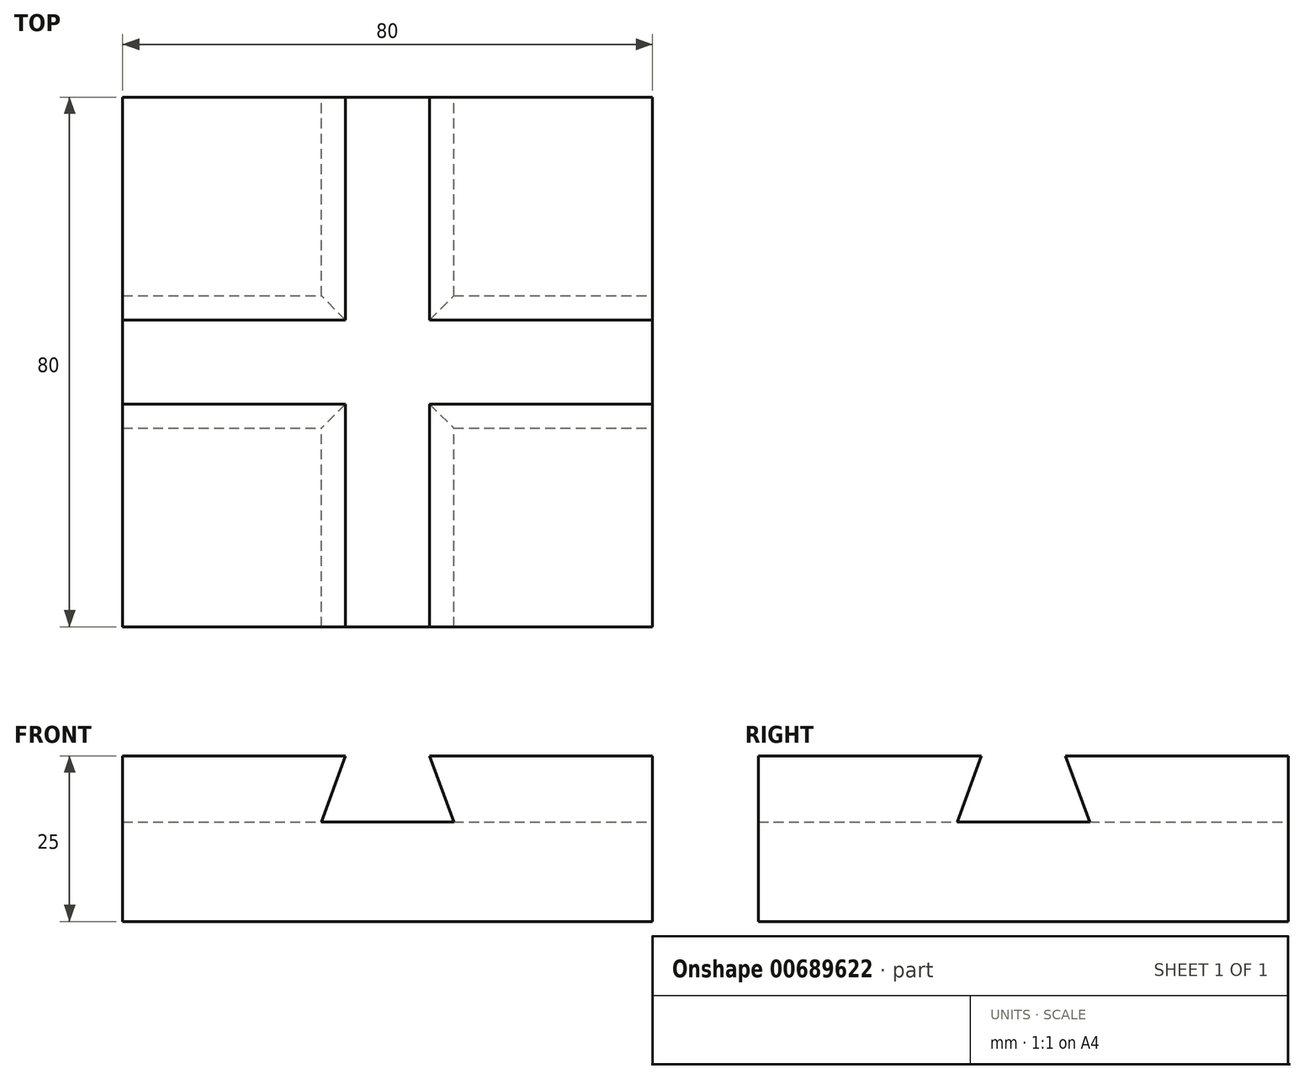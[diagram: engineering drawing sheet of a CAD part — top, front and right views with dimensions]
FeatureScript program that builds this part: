
annotation { "Feature Type Name" : "Feature", "Feature Type Description" : "" }
export const myFeature = defineFeature(function(context is Context, id is Id, definition is map)
    precondition{}
    {
        {
            var Q0;
            Q0=qCreatedBy(makeId("Front.planeOp"),FACE);
            var sketch = newSketch(context, id + "F0", { "sketchPlane" : qUnion([Q0])});
            skLineSegment(sketch, "E0.bottom", {"start": v(-11.36, -2.73) * mm, "end": v(-91.36, -2.73) * mm});
            skLineSegment(sketch, "E0.top", {"start": v(-11.36, 22.27) * mm, "end": v(-45, 22.27) * mm});
            skLineSegment(sketch, "E0.left", {"start": v(-11.36, -2.73) * mm, "end": v(-11.36, 22.27) * mm});
            skLineSegment(sketch, "E0.right", {"start": v(-91.36, -2.73) * mm, "end": v(-91.36, 22.27) * mm});
            skLineSegment(sketch, "E1.bottom", {"start": v(-61.36, 12.27) * mm, "end": v(-41.36, 12.27) * mm});
            skLineSegment(sketch, "E2", {"start": v(-57.72, 22.27) * mm, "end": v(-61.36, 12.27) * mm});
            skLineSegment(sketch, "E3", {"start": v(-45, 22.27) * mm, "end": v(-41.36, 12.27) * mm});
            skLineSegment(sketch, "E4.trimOffspring", {"start": v(-57.72, 22.27) * mm, "end": v(-91.36, 22.27) * mm});
            skSolve(sketch);
        }
        {
            var Q0;
            Q0=makeQuery(id+"F0.imprint","IMPRINT",FACE,{"disambiguationData":[TD([[makeQuery(id+"F0.imprint","IMPRINT",EDGE,{"derivedFrom":sQuery(id+"F0.wireOp",EDGE,"E0.bottom")}),-1.0]])]});
            extrude(context, id + "F1", {"entities" : qUnion([Q0]), "depth" : 80 * mm, "offsetDistance" : 25 * mm});
        }
        {
            var Q0;
            Q0=makeQuery(id+"F1.opExtrude","SWEPT_FACE",FACE,{"disambiguationData":[OSD([sQuery(id+"F0.wireOp",EDGE,"E0.left")])]});
            var sketch = newSketch(context, id + "F2", { "sketchPlane" : qUnion([Q0])});
            skLineSegment(sketch, "E5.bottom", {"start": v(-50, 12.27) * mm, "end": v(-30, 12.27) * mm});
            skPoint(sketch, "E5.middle", {"position": v(-40, 22.27) * mm});
            skLineSegment(sketch, "E6", {"start": v(-40, 22.27) * mm, "end": v(-46.36, 22.27) * mm});
            skLineSegment(sketch, "E7", {"start": v(-40, 22.27) * mm, "end": v(-33.64, 22.27) * mm});
            skLineSegment(sketch, "E8", {"start": v(-46.36, 22.27) * mm, "end": v(-50, 12.27) * mm});
            skLineSegment(sketch, "E9", {"start": v(-33.64, 22.27) * mm, "end": v(-30, 12.27) * mm});
            skSolve(sketch);
        }
        {
            var Q0;
            Q0=makeQuery(id+"F2.imprint","IMPRINT",FACE,{"disambiguationData":[TD([[makeQuery(id+"F2.imprint","IMPRINT",EDGE,{"derivedFrom":sQuery(id+"F2.wireOp",EDGE,"E5.bottom")}),1.0]])]});
            extrude(context, id + "F3", {"entities" : qUnion([Q0]), "operationType" : NewBodyOperationType.REMOVE, "oppositeDirection" : true, "depth" : 80 * mm, "offsetDistance" : 25 * mm});
        }
    });
